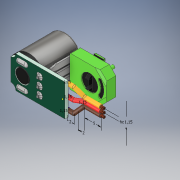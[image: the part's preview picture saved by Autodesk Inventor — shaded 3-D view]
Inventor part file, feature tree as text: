
AUTODESK INVENTOR PART (.ipt)
format: ipt  version: 2019 (Build 230136000, 136)  size: 1,630,208 bytes
history: native  units: mm
features: extrude x29, sketch x25, fillet x14, projected_geometry x12, plane x8, chamfer x8, reference x4, mirror x3, sweep x3, other x3, pattern_linear x2
ambient origin geometry x8: Origin, YZ Plane, XZ Plane, XY Plane, X Axis, Y Axis, Z Axis, Center Point
bodies: Solid1 (feature_tree)
feature tree (111):
  extrude  "Extrusion1"  Depth=9.75mm
  extrude  "Extrusion2"  Depth=3.5mm
  sketch  "Sketch3"  dims[d4=4.0mm d5=4.5mm]
  extrude  "Extrusion3"  Depth=4.5mm
  extrude  "Extrusion4"  Depth=10.0mm
  extrude  "Extrusion5"  Depth=12.25mm TaperAngle=0.0deg
  extrude  "Extrusion6"  Depth=0.75mm
  extrude  "Extrusion7"  Depth=3.0mm TaperAngle=0.0deg
  sketch  "Sketch6"  dims[d12=4.0mm d13=0.75mm]
  extrude  "Extrusion8"  Depth=6.5mm
  extrude  "Extrusion9"  Depth=1.5mm
  extrude  "Extrusion11"  Depth=1.0mm TaperAngle=0.0deg
  fillet  "Fillet2"  Radius=0.6mm
  fillet  "Fillet3"  Radius=4.5mm
  plane  "Work Plane1"
  mirror  "Mirror1"
  fillet  "Fillet4"  Radius=3.4mm
  extrude  "Extrusion12"  Depth=0.25mm TaperAngle=0.0deg
  chamfer  "Chamfer1"  Distance=1.0mm
  chamfer  "Chamfer2"  Distance=0.75mm
  chamfer  "Chamfer3"  Distance=0.25mm
  chamfer  "Chamfer4"  Distance=0.25mm
  plane  "Work Plane2"
  extrude  "Extrusion13"  Depth=0.25mm
  fillet  "Fillet6"  Radius=0.4mm
  pattern_linear  "Rectangular Pattern1"  Spacing1=5.0mm  [1 undecoded]
  mirror  "Mirror2"
  extrude  "Extrusion14"  Depth=1.5mm
  fillet  "Fillet8"  Radius=1.5mm
  plane  "Work Plane3"
  extrude  "Extrusion15"  Depth=0.25mm TaperAngle=45.0deg
  fillet  "Fillet9"  Radius=0.25mm
  pattern_linear  "Rectangular Pattern2"  Spacing1=0.25mm  [1 undecoded]
  fillet  "Fillet10"  Radius=0.25mm
  fillet  "Fillet11"  [1 undecoded]
  plane  "Work Plane4"
  extrude  "Extrusion16"  Depth=0.4mm
  fillet  "Fillet12"  Radius=2.0mm
  chamfer  "Chamfer5"  Distance=0.05mm
  chamfer  "Chamfer6"  Distance=0.5mm
  sketch  "Sketch13"  dims[d36=1.5mm]
  extrude  "Extrusion17"  Depth=0.5mm
  extrude  "Extrusion18"  Depth=40.0mm
  sketch  "Sketch14"  dims[d37=2.25mm]
  extrude  "Extrusion19"  Depth=1.5mm
  extrude  "Extrusion20"  Depth=7.0mm
  sketch  "Sketch15"  dims[d39=2.0mm d40=0.75mm d41=0.0mm d42=0.25mm d43=0.0mm d50=0.25mm d51=0.0mm]
  extrude  "Extrusion21"  Depth=3.5mm
  extrude  "Extrusion22"  Depth=2.0mm
  extrude  "Extrusion23"  Depth=0.5mm TaperAngle=0.0deg
  extrude  "Extrusion24"  Depth=0.7mm
  plane  "Work Plane5"
  extrude  "Extrusion26"  [1 undecoded]
  chamfer  "Chamfer7"  Distance=0.75mm
  fillet  "Fillet13"  Radius=1.65mm
  mirror  "Mirror3"
  extrude  "Extrusion27"  Depth=2.0mm
  chamfer  "Chamfer8"  Distance=2.0mm
  fillet  "Fillet14"  Radius=9.0mm
  sketch  "Sketch19"  dims[d58=0.1mm]
  extrude  "Extrusion30"  Depth=2.0mm
  extrude  "Extrusion31"  Depth=0.75mm
  plane  "Work Plane7"
  sketch  "Sketch23"  dims[d61=0.5mm]
  plane  "Work Plane8"
  sketch  "Sketch24"  dims[d62=0.05mm]
  sketch  "3D Sketch2"
  plane  "Work Plane9"
  sketch  "Sketch25"  dims[d63=0.1mm d64=0.15mm]
  sweep  "Sweep4"
  sweep  "Sweep5"
  sweep  "Sweep6"
  fillet  "Fillet17"  Radius=0.1mm
  extrude  "Extrusion32"  Depth=0.6mm
  fillet  "Fillet18"  Radius=0.25mm
  fillet  "Fillet19"  Radius=7.5mm
  extrude  "Extrusion33"  Depth=9.6mm
  sketch  "Sketch1"  dims[d0=16.5mm d1=9.75mm]
  sketch  "Sketch2"  dims[d2=3.0mm d3=3.5mm]
  sketch  "Sketch4"  dims[d6=1.0mm d7=0.0mm d8=10.0mm]
  sketch  "Sketch5"  dims[d9=8.0mm d10=12.25mm d11=0.0mm]
  projected_geometry  "Projected Loop1"
  sketch  "Sketch7"  dims[d14=0.5mm d15=0.0mm d16=3.0mm d17=0.0mm]
  sketch  "Sketch8"  dims[d18=1.0mm d19=6.5mm]
  sketch  "Sketch9"  dims[d20=1.25mm d21=1.5mm]
  sketch  "Sketch10"  dims[d22=1.75mm d24=1.0mm d25=0.0mm d26=0.6mm d27=4.5mm d28=3.4mm]
  projected_geometry  "Projected Loop2"
  projected_geometry  "Projected Loop3"
  sketch  "Sketch11"  dims[d30=6.5mm d31=0.25mm d32=0.0mm]
  sketch  "Sketch12"  dims[d33=0.01mm d34=1.0mm d35=0.0mm]
  projected_geometry  "Projected Loop4"
  projected_geometry  "Projected Loop5"
  projected_geometry  "Projected Loop6"
  sketch  "Sketch17"  dims[d54=0.1mm d55=0.25mm d56=0.4mm]
  projected_geometry  "Projected Loop7"
  sketch  "Sketch18"  dims[d57=0.75mm]
  sketch  "Sketch21"  dims[d59=1.25mm]
  sketch  "Sketch22"  dims[d60=0.25mm]
  reference  "Reference1"
  reference  "Reference2"
  reference  "Reference3"
  reference  "Reference4"
  sketch  "Sketch26"  dims[d66=4.0mm d67=5.0mm d68=1.5mm d69=1.5mm d70=0.0mm d71=0.25mm d72=0.75mm d73=45.0deg d74=0.25mm d75=0.75mm d76=45.0deg d77=0.25mm d78=0.75mm d79=45.0deg d80=0.25mm d81=0.75mm d82=45.0deg d83=-0.5mm d84=0.4mm d85=2.0mm d86=0.05mm d87=0.5mm d88=0.0mm d89=0.5mm d90=0.25mm d92=40.0mm d94=1.333333mm d95=1.5mm d96=7.0mm d97=3.5mm d98=2.0mm d99=0.5mm d100=0.0mm d101=0.7mm d102=-7.75mm d103=0.75mm d104=1.65mm d105=2.0mm d106=2.0mm d107=9.0mm d108=2.0mm d109=0.75mm d110=0.5mm d111=0.0mm d112=2.0mm d113=30.0mm d115=2.5mm d116=0.1mm d117=0.6mm d118=0.25mm d119=7.5mm d120=9.6mm d121=11.0mm d122=2.0mm d123=2.0mm d124=2.0mm d125=2.0mm d126=3.0mm d127=0.0mm d128=0.5mm d129=0.25mm d130=1.0mm d131=45.0deg d132=0.25mm d133=1.0mm d134=45.0deg d135=5.0mm d137=1.1mm d138=4.25mm d139=0.75mm d140=0.25mm d141=0.0mm d142=0.25mm d143=0.0mm d144=8.25mm d145=0.05mm d146=0.5mm d148=5.0mm d149=1.0mm d150=0.0mm d151=2.5mm d152=0.0mm d153=6.5mm d154=5.75mm d155=2.5mm d156=1.0mm d157=0.25mm d158=0.25mm d159=0.3mm d160=0.3mm d161=0.6mm d162=0.55mm d163=0.15mm d164=0.0mm d165=0.1mm d166=0.0mm d167=0.1mm d168=0.0mm d169=0.5mm d170=0.0mm d177=0.5mm d182=-5.5mm d185=0.5mm d186=0.5mm d187=0.5mm d188=0.1mm d189=3.0mm d190=0.0mm d191=0.5mm d192=0.5mm d193=45.0deg d194=0.1mm d195=0.75mm d196=1.0mm d197=0.0mm d198=0.5mm d199=0.5mm d200=45.0deg d202=0.1mm d203=0.25mm d204=3.5mm d205=0.75mm d206=1.0mm d228=0.5mm d229=6.0mm d230=0.5mm d231=0.4mm d232=0.0mm d233=0.3mm d234=0.3mm d235=0.25mm d236=1.0mm d237=1.0mm d238=1.0mm d239=0.5mm d240=0.5mm d241=1.0mm d242=0.0mm d243=0.5mm d244=2.0mm d245=1.75mm d246=1.15mm d247=1.15mm d248=2.0mm d249=5.0mm d250=1.15mm d251=1.15mm d252=1.15mm d253=0.0mm d254=0.0mm d255=0.0mm d256=0.0mm d257=0.0mm d258=0.0mm d259=0.5mm d260=0.5mm d261=0.0mm d262=0.25mm d263=0.2mm d264=0.75mm d265=1.0mm d266=0.0mm]
  projected_geometry  "Projected Loop8"
  projected_geometry  "Projected Loop9"
  projected_geometry  "Projected Loop10"
  projected_geometry  "Project Cut Edges1"
  projected_geometry  "Project Cut Edges3"
  other  "<userpath>\OneDrive\Documenten\Inventor\servo\Assembly1.iam"
  other  "Assembly1.iam"
  other  "servo midden:1"
note: 4 required parameter values undecoded (feature->parameter linkage not recoverable at this tier; creation-order binding heuristic only, values carry confidence <= 0.55)
